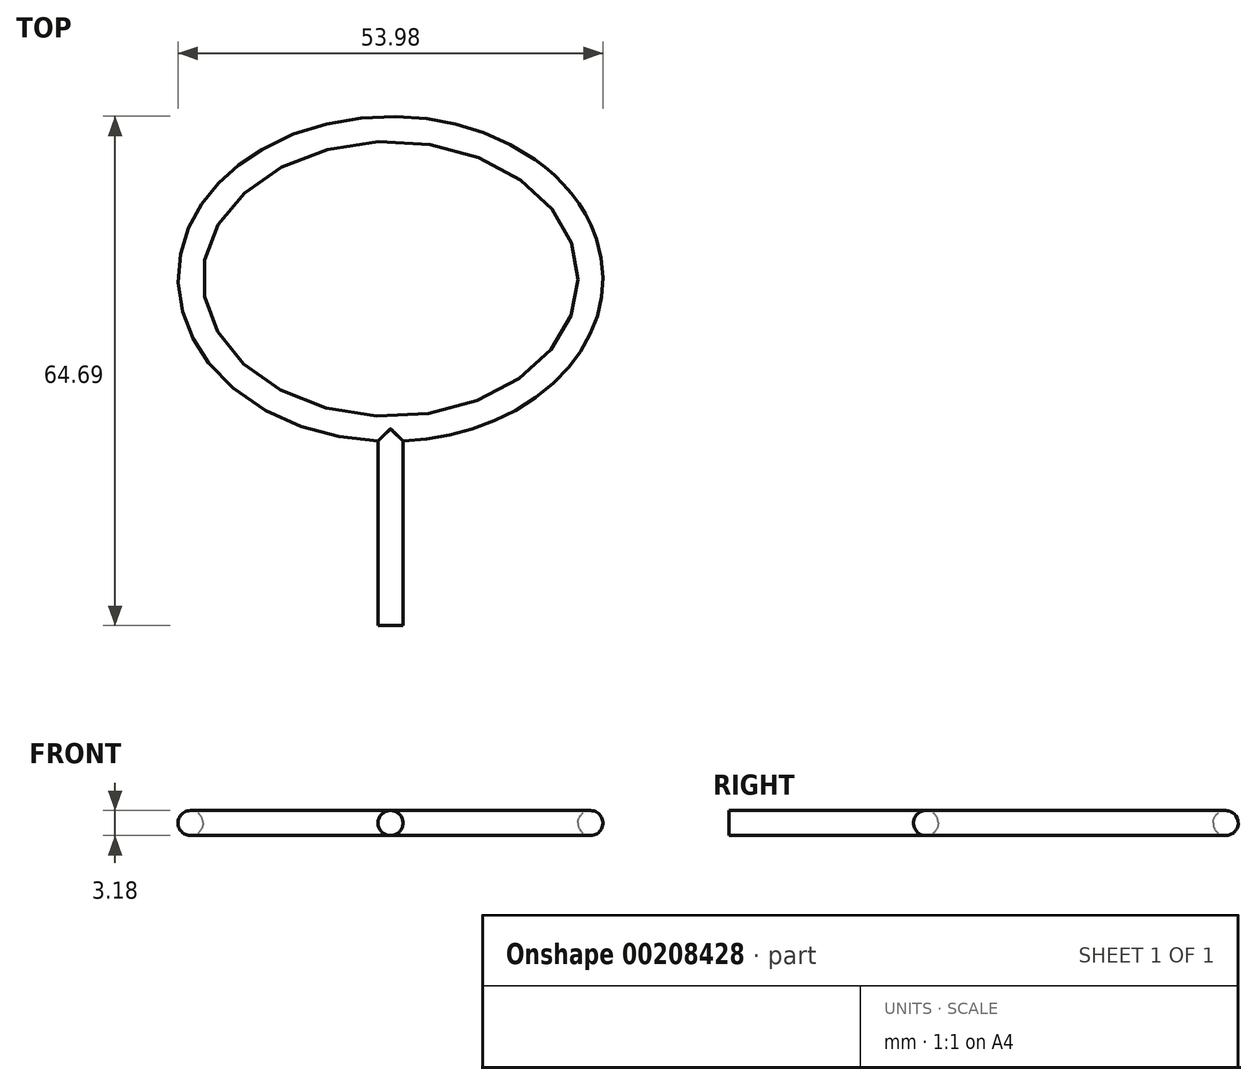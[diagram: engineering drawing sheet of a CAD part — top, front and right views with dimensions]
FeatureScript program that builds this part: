
annotation { "Feature Type Name" : "Feature", "Feature Type Description" : "" }
export const myFeature = defineFeature(function(context is Context, id is Id, definition is map)
    precondition{}
    {
        {
            var Q0;
            Q0=qCreatedBy(makeId("Top.planeOp"),FACE);
            var sketch = newSketch(context, id + "F0", { "sketchPlane" : qUnion([Q0])});
            skEllipse(sketch, "E0", {"center": v(0, 0) * mm, "majorRadius": 25.4 * mm, "minorRadius": 19.05 * mm, "majorAxis": v(-1, 0)});
            skSolve(sketch);
        }
        {
            var Q0;
            Q0=qCreatedBy(makeId("Front.planeOp"),FACE);
            var sketch = newSketch(context, id + "F1", { "sketchPlane" : qUnion([Q0])});
            skLineSegment(sketch, "E1.0", {"start": v(25.4, 0) * mm, "end": v(-25.4, 0) * mm});
            skCircle(sketch, "E2", {"center": v(-25.4, 0) * mm, "radius": 1.59 * mm});
            skSolve(sketch);
        }
        {
            var Q0;
            Q0=makeQuery(id+"F1.imprint","IMPRINT",FACE,{"disambiguationData":[TD([[makeQuery(id+"F1.imprint","IMPRINT",EDGE,{"derivedFrom":sQuery(id+"F1.wireOp",EDGE,"E2")}),1.0]])]});
            var Q1;
            Q1=sQuery(id+"F0.wireOp",EDGE,"E0");
            sweep(context, id + "F2", {"profiles" : qUnion([Q0]), "path" : qUnion([Q1])});
        }
        {
            var Q0;
            Q0=qCreatedBy(makeId("Front.planeOp"),FACE);
            cPlane(context, id + "F3", {"entities" : qUnion([Q0]), "cplaneType" : CPlaneType.OFFSET, "offset" : 19.05 * mm, "width" : 150 * mm, "height" : 150 * mm});
        }
        {
            var Q0;
            Q0=qCreatedBy(id+"F3.planeOp",FACE);
            var sketch = newSketch(context, id + "F4", { "sketchPlane" : qUnion([Q0])});
            skCircle(sketch, "E3", {"center": v(0, 0) * mm, "radius": 1.59 * mm});
            skSolve(sketch);
        }
        {
            var Q0;
            Q0=qSketchRegion(id+"F4",true);
            extrude(context, id + "F5", {"entities" : qUnion([Q0]), "operationType" : NewBodyOperationType.ADD, "depth" : 25 * mm});
        }
    });
